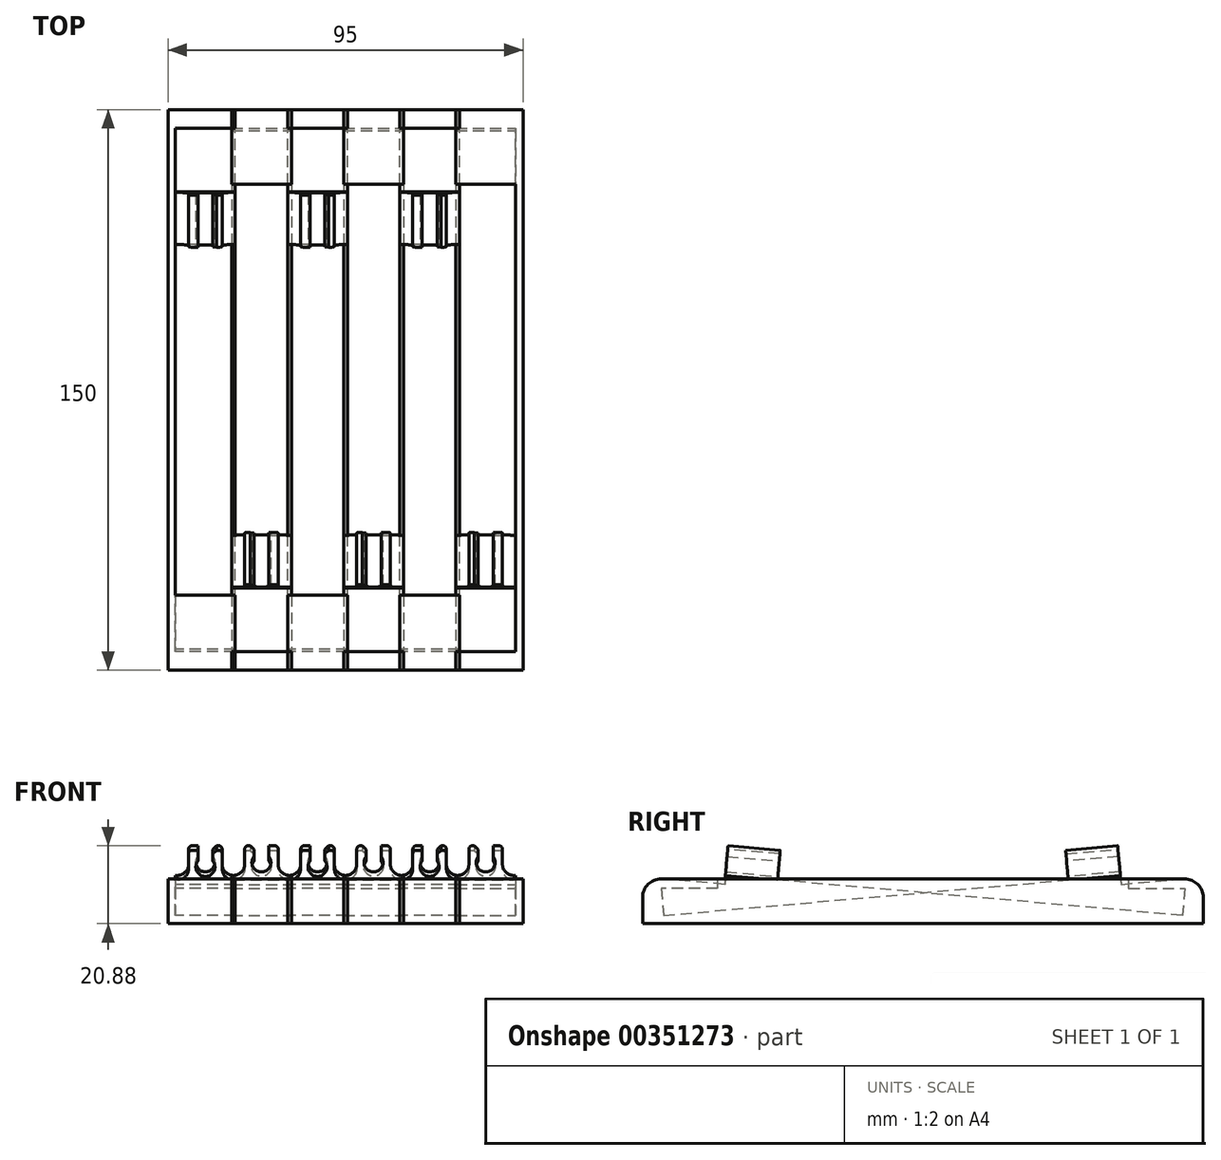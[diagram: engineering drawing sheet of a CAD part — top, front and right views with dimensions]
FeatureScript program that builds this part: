
annotation { "Feature Type Name" : "Feature", "Feature Type Description" : "" }
export const myFeature = defineFeature(function(context is Context, id is Id, definition is map)
    precondition{}
    {
        {
            var Q0;
            Q0=qCreatedBy(makeId("Right.planeOp"),FACE);
            var sketch = newSketch(context, id + "F0", { "sketchPlane" : qUnion([Q0])});
            skLineSegment(sketch, "E0", {"start": v(0, 0) * mm, "end": v(0, 7) * mm});
            skLineSegment(sketch, "E1", {"start": v(5, 12) * mm, "end": v(20, 12) * mm});
            skLineSegment(sketch, "E2", {"start": v(20, 12) * mm, "end": v(20, 9.5) * mm});
            skLineSegment(sketch, "E3", {"start": v(20, 9.5) * mm, "end": v(5.06, 8.2) * mm, "construction": true});
            skLineSegment(sketch, "E4", {"start": v(4.94, 9.5) * mm, "end": v(5.58, 2.22) * mm});
            skLineSegment(sketch, "E5", {"start": v(5.58, 2.22) * mm, "end": v(113.9, 11.7) * mm});
            skLineSegment(sketch, "E6", {"start": v(150, 7) * mm, "end": v(150, 0) * mm});
            skLineSegment(sketch, "E7", {"start": v(150, 0) * mm, "end": v(0, 0) * mm});
            skLineSegment(sketch, "E8", {"start": v(113.9, 11.7) * mm, "end": v(113.2, 19.66) * mm});
            skLineSegment(sketch, "E9", {"start": v(113.2, 19.66) * mm, "end": v(127.14, 20.88) * mm});
            skLineSegment(sketch, "E10", {"start": v(127.14, 20.88) * mm, "end": v(128.05, 10.52) * mm});
            skPoint(sketch, "E11.visualSharp", {"position": v(0, 12) * mm});
            skArc(sketch, "E11.filletArc", {"start": v(5, 12) * mm, "mid": v(1.46, 10.54) * mm, "end": v(0, 7) * mm});
            skPoint(sketch, "E12.visualSharp", {"position": v(150, 12) * mm});
            skLineSegment(sketch, "E13", {"start": v(20, 9.5) * mm, "end": v(4.94, 9.5) * mm});
            skLineSegment(sketch, "E14", {"start": v(128.05, 10.52) * mm, "end": v(145, 12) * mm});
            skLineSegment(sketch, "E15", {"start": v(145, 12) * mm, "end": v(145, 12) * mm});
            skArc(sketch, "E16.filletArc", {"start": v(150, 7) * mm, "mid": v(148.54, 10.54) * mm, "end": v(145, 12) * mm});
            skSolve(sketch);
        }
        {
            var Q0;
            Q0=qSketchRegion(id+"F0",true);
            extrude(context, id + "F1", {"entities" : qUnion([Q0]), "depth" : 16 * mm});
        }
        {
            var Q0;
            Q0=makeQuery(id+"F1.opExtrude","SWEPT_FACE",FACE,{"disambiguationData":[OSD([sQuery(id+"F0.wireOp",EDGE,"E8")])]});
            var sketch = newSketch(context, id + "F2", { "sketchPlane" : qUnion([Q0])});
            skLineSegment(sketch, "E17", {"start": v(8, 1.72) * mm, "end": v(8, 9.72) * mm, "construction": true});
            skArc(sketch, "E18", {"start": v(6, 6.8) * mm, "mid": v(8, 2.67) * mm, "end": v(10, 6.8) * mm});
            skLineSegment(sketch, "E19", {"start": v(12.5, 8.72) * mm, "end": v(12.5, 4.72) * mm});
            skLineSegment(sketch, "E20", {"start": v(15.5, 1.72) * mm, "end": v(18.5, 1.72) * mm});
            skLineSegment(sketch, "E21", {"start": v(18.5, 1.72) * mm, "end": v(18.5, 10.72) * mm});
            skLineSegment(sketch, "E22", {"start": v(3.5, 8.72) * mm, "end": v(3.5, 4.72) * mm});
            skLineSegment(sketch, "E23", {"start": v(0.5, 1.72) * mm, "end": v(-2.5, 1.72) * mm});
            skLineSegment(sketch, "E24", {"start": v(-2.5, 1.72) * mm, "end": v(-2.5, 10.72) * mm});
            skLineSegment(sketch, "E25", {"start": v(-2.5, 10.72) * mm, "end": v(18.5, 10.72) * mm});
            skLineSegment(sketch, "E26", {"start": v(8, 5.22) * mm, "end": v(6, 5.22) * mm, "construction": true});
            skLineSegment(sketch, "E27", {"start": v(6, 6.8) * mm, "end": v(6, 9.72) * mm});
            skLineSegment(sketch, "E28", {"start": v(8, 5.22) * mm, "end": v(10, 5.22) * mm, "construction": true});
            skLineSegment(sketch, "E29", {"start": v(10, 6.8) * mm, "end": v(10, 9.72) * mm});
            skPoint(sketch, "E30.orphan", {"position": v(3.5, 5.22) * mm});
            skPoint(sketch, "E31.orphan", {"position": v(12.5, 5.22) * mm});
            skLineSegment(sketch, "E32", {"start": v(6, 9.72) * mm, "end": v(4.5, 9.72) * mm});
            skLineSegment(sketch, "E33", {"start": v(10, 9.72) * mm, "end": v(11.5, 9.72) * mm});
            skPoint(sketch, "E34.visualSharp", {"position": v(3.5, 1.72) * mm});
            skArc(sketch, "E34.filletArc", {"start": v(0.5, 1.72) * mm, "mid": v(2.62, 2.6) * mm, "end": v(3.5, 4.72) * mm});
            skPoint(sketch, "E35.visualSharp", {"position": v(12.5, 1.72) * mm});
            skArc(sketch, "E35.filletArc", {"start": v(12.5, 4.72) * mm, "mid": v(13.38, 2.6) * mm, "end": v(15.5, 1.72) * mm});
            skPoint(sketch, "E36.visualSharp", {"position": v(3.5, 9.72) * mm});
            skArc(sketch, "E36.filletArc", {"start": v(4.5, 9.72) * mm, "mid": v(3.8, 9.43) * mm, "end": v(3.5, 8.72) * mm});
            skPoint(sketch, "E37.visualSharp", {"position": v(12.5, 9.72) * mm});
            skArc(sketch, "E37.filletArc", {"start": v(12.5, 8.72) * mm, "mid": v(12.2, 9.43) * mm, "end": v(11.5, 9.72) * mm});
            skSolve(sketch);
        }
        {
            var Q0;
            Q0=qSketchRegion(id+"F2",true);
            extrude(context, id + "F3", {"entities" : qUnion([Q0]), "operationType" : NewBodyOperationType.REMOVE, "oppositeDirection" : true, "depth" : 25 * mm});
        }
        {
            var Q0;
            Q0=makeQuery(id+"F3.boolean.opBoolean","COPY",EDGE,{"derivedFrom":makeQuery(id+"F3.opExtrude","SWEPT_EDGE",EDGE,{"disambiguationData":[OSD([sQuery(id+"F0.wireOp",EDGE,"E8"),sQuery(id+"F0.wireOp",EDGE,"E9"),sQuery(id+"F2.wireOp",EDGE,"E27"),sQuery(id+"F2.wireOp",EDGE,"E32")])]})});
            var Q1;
            Q1=makeQuery(id+"F3.boolean.opBoolean","COPY",EDGE,{"derivedFrom":makeQuery(id+"F3.opExtrude","SWEPT_EDGE",EDGE,{"disambiguationData":[OSD([sQuery(id+"F0.wireOp",EDGE,"E8"),sQuery(id+"F0.wireOp",EDGE,"E9"),sQuery(id+"F2.wireOp",EDGE,"E29"),sQuery(id+"F2.wireOp",EDGE,"E33")])]})});
            chamfer(context, id + "F4", {"entities" : qUnion([Q0, Q1]), "width" : 1 * mm, "tangentPropagation" : true});
        }
        {
            var Q0;
            Q0=makeQuery(id+"F1.opExtrude","SWEPT_BODY",BODY,{"disambiguationData":[OSD([sQuery(id+"F0.wireOp",EDGE,"E0"),sQuery(id+"F0.wireOp",EDGE,"E1"),sQuery(id+"F0.wireOp",EDGE,"E2"),sQuery(id+"F0.wireOp",EDGE,"E4"),sQuery(id+"F0.wireOp",EDGE,"E5"),sQuery(id+"F0.wireOp",EDGE,"E6"),sQuery(id+"F0.wireOp",EDGE,"E7"),sQuery(id+"F0.wireOp",EDGE,"E8"),sQuery(id+"F0.wireOp",EDGE,"E9"),sQuery(id+"F0.wireOp",EDGE,"E10"),sQuery(id+"F0.wireOp",EDGE,"Y9S6pfHg-R41R-CDvD-xWL7-1D2eYxtCf16d"),sQuery(id+"F0.wireOp",EDGE,"E11.filletArc"),sQuery(id+"F0.wireOp",EDGE,"E12.filletArc"),sQuery(id+"F0.wireOp",EDGE,"E13")])]});
            transform(context, id + "F5", {"entities" : qUnion([Q0]), "transformType" : TransformType.TRANSLATION_3D, "dx" : 30 * mm, "dy" : 0 * mm, "dz" : 0 * mm, "makeCopy" : true});
        }
        {
            var Q0;
            Q0=makeQuery(id+"F5.opPattern","COPY",BODY,{"derivedFrom":makeQuery(id+"F1.opExtrude","SWEPT_BODY",BODY,{"disambiguationData":[OSD([sQuery(id+"F0.wireOp",EDGE,"E0"),sQuery(id+"F0.wireOp",EDGE,"E1"),sQuery(id+"F0.wireOp",EDGE,"E2"),sQuery(id+"F0.wireOp",EDGE,"E4"),sQuery(id+"F0.wireOp",EDGE,"E5"),sQuery(id+"F0.wireOp",EDGE,"E6"),sQuery(id+"F0.wireOp",EDGE,"E7"),sQuery(id+"F0.wireOp",EDGE,"E8"),sQuery(id+"F0.wireOp",EDGE,"E9"),sQuery(id+"F0.wireOp",EDGE,"E10"),sQuery(id+"F0.wireOp",EDGE,"Y9S6pfHg-R41R-CDvD-xWL7-1D2eYxtCf16d"),sQuery(id+"F0.wireOp",EDGE,"E11.filletArc"),sQuery(id+"F0.wireOp",EDGE,"E12.filletArc"),sQuery(id+"F0.wireOp",EDGE,"E13")])]}),"instanceName":"1"});
            transform(context, id + "F6", {"entities" : qUnion([Q0]), "transformType" : TransformType.TRANSLATION_3D, "dx" : 30 * mm, "dy" : 0 * mm, "dz" : 0 * mm, "makeCopy" : true});
        }
        {
            var Q0;
            Q0=makeQuery(id+"F1.opExtrude","SWEPT_BODY",BODY,{"disambiguationData":[OSD([sQuery(id+"F0.wireOp",EDGE,"E0"),sQuery(id+"F0.wireOp",EDGE,"E1"),sQuery(id+"F0.wireOp",EDGE,"E2"),sQuery(id+"F0.wireOp",EDGE,"E4"),sQuery(id+"F0.wireOp",EDGE,"E5"),sQuery(id+"F0.wireOp",EDGE,"E6"),sQuery(id+"F0.wireOp",EDGE,"E7"),sQuery(id+"F0.wireOp",EDGE,"E8"),sQuery(id+"F0.wireOp",EDGE,"E9"),sQuery(id+"F0.wireOp",EDGE,"E10"),sQuery(id+"F0.wireOp",EDGE,"Y9S6pfHg-R41R-CDvD-xWL7-1D2eYxtCf16d"),sQuery(id+"F0.wireOp",EDGE,"E11.filletArc"),sQuery(id+"F0.wireOp",EDGE,"E12.filletArc"),sQuery(id+"F0.wireOp",EDGE,"E13")])]});
            transform(context, id + "F7", {"entities" : qUnion([Q0]), "transformType" : TransformType.TRANSLATION_3D, "dx" : 0 * mm, "dy" : 160 * mm, "dz" : 0 * mm, "makeCopy" : true});
        }
        {
            var Q0;
            Q0=makeQuery(id+"F5.opPattern","COPY",BODY,{"derivedFrom":makeQuery(id+"F1.opExtrude","SWEPT_BODY",BODY,{"disambiguationData":[OSD([sQuery(id+"F0.wireOp",EDGE,"E0"),sQuery(id+"F0.wireOp",EDGE,"E1"),sQuery(id+"F0.wireOp",EDGE,"E2"),sQuery(id+"F0.wireOp",EDGE,"E4"),sQuery(id+"F0.wireOp",EDGE,"E5"),sQuery(id+"F0.wireOp",EDGE,"E6"),sQuery(id+"F0.wireOp",EDGE,"E7"),sQuery(id+"F0.wireOp",EDGE,"E8"),sQuery(id+"F0.wireOp",EDGE,"E9"),sQuery(id+"F0.wireOp",EDGE,"E10"),sQuery(id+"F0.wireOp",EDGE,"Y9S6pfHg-R41R-CDvD-xWL7-1D2eYxtCf16d"),sQuery(id+"F0.wireOp",EDGE,"E11.filletArc"),sQuery(id+"F0.wireOp",EDGE,"E12.filletArc"),sQuery(id+"F0.wireOp",EDGE,"E13")])]}),"instanceName":"1"});
            transform(context, id + "F8", {"entities" : qUnion([Q0]), "transformType" : TransformType.TRANSLATION_3D, "dx" : 0 * mm, "dy" : 160 * mm, "dz" : 0 * mm, "makeCopy" : true});
        }
        {
            var Q0;
            Q0=makeQuery(id+"F6.opPattern","COPY",BODY,{"derivedFrom":makeQuery(id+"F5.opPattern","COPY",BODY,{"derivedFrom":makeQuery(id+"F1.opExtrude","SWEPT_BODY",BODY,{"disambiguationData":[OSD([sQuery(id+"F0.wireOp",EDGE,"E0"),sQuery(id+"F0.wireOp",EDGE,"E1"),sQuery(id+"F0.wireOp",EDGE,"E2"),sQuery(id+"F0.wireOp",EDGE,"E4"),sQuery(id+"F0.wireOp",EDGE,"E5"),sQuery(id+"F0.wireOp",EDGE,"E6"),sQuery(id+"F0.wireOp",EDGE,"E7"),sQuery(id+"F0.wireOp",EDGE,"E8"),sQuery(id+"F0.wireOp",EDGE,"E9"),sQuery(id+"F0.wireOp",EDGE,"E10"),sQuery(id+"F0.wireOp",EDGE,"Y9S6pfHg-R41R-CDvD-xWL7-1D2eYxtCf16d"),sQuery(id+"F0.wireOp",EDGE,"E11.filletArc"),sQuery(id+"F0.wireOp",EDGE,"E12.filletArc"),sQuery(id+"F0.wireOp",EDGE,"E13")])]}),"instanceName":"1"}),"instanceName":"1"});
            transform(context, id + "F9", {"entities" : qUnion([Q0]), "transformType" : TransformType.TRANSLATION_3D, "dx" : 0 * mm, "dy" : 160 * mm, "dz" : 0 * mm, "makeCopy" : true});
        }
        {
            var Q0;
            Q0=qCreatedBy(makeId("Right.planeOp"),FACE);
            var sketch = newSketch(context, id + "F10", { "sketchPlane" : qUnion([Q0])});
            skLineSegment(sketch, "E38", {"start": v(0, 0) * mm, "end": v(0, 50) * mm, "construction": true});
            skSolve(sketch);
        }
        {
            var Q0;
            Q0=makeQuery(id+"F8.opPattern","COPY",BODY,{"derivedFrom":makeQuery(id+"F5.opPattern","COPY",BODY,{"derivedFrom":makeQuery(id+"F1.opExtrude","SWEPT_BODY",BODY,{"disambiguationData":[OSD([sQuery(id+"F0.wireOp",EDGE,"E0"),sQuery(id+"F0.wireOp",EDGE,"E1"),sQuery(id+"F0.wireOp",EDGE,"E2"),sQuery(id+"F0.wireOp",EDGE,"E4"),sQuery(id+"F0.wireOp",EDGE,"E5"),sQuery(id+"F0.wireOp",EDGE,"E6"),sQuery(id+"F0.wireOp",EDGE,"E7"),sQuery(id+"F0.wireOp",EDGE,"E8"),sQuery(id+"F0.wireOp",EDGE,"E9"),sQuery(id+"F0.wireOp",EDGE,"E10"),sQuery(id+"F0.wireOp",EDGE,"Y9S6pfHg-R41R-CDvD-xWL7-1D2eYxtCf16d"),sQuery(id+"F0.wireOp",EDGE,"E11.filletArc"),sQuery(id+"F0.wireOp",EDGE,"E12.filletArc"),sQuery(id+"F0.wireOp",EDGE,"E13")])]}),"instanceName":"1"}),"instanceName":"1"});
            var Q1;
            Q1=makeQuery(id+"F9.opPattern","COPY",BODY,{"derivedFrom":makeQuery(id+"F6.opPattern","COPY",BODY,{"derivedFrom":makeQuery(id+"F5.opPattern","COPY",BODY,{"derivedFrom":makeQuery(id+"F1.opExtrude","SWEPT_BODY",BODY,{"disambiguationData":[OSD([sQuery(id+"F0.wireOp",EDGE,"E0"),sQuery(id+"F0.wireOp",EDGE,"E1"),sQuery(id+"F0.wireOp",EDGE,"E2"),sQuery(id+"F0.wireOp",EDGE,"E4"),sQuery(id+"F0.wireOp",EDGE,"E5"),sQuery(id+"F0.wireOp",EDGE,"E6"),sQuery(id+"F0.wireOp",EDGE,"E7"),sQuery(id+"F0.wireOp",EDGE,"E8"),sQuery(id+"F0.wireOp",EDGE,"E9"),sQuery(id+"F0.wireOp",EDGE,"E10"),sQuery(id+"F0.wireOp",EDGE,"Y9S6pfHg-R41R-CDvD-xWL7-1D2eYxtCf16d"),sQuery(id+"F0.wireOp",EDGE,"E11.filletArc"),sQuery(id+"F0.wireOp",EDGE,"E12.filletArc"),sQuery(id+"F0.wireOp",EDGE,"E13")])]}),"instanceName":"1"}),"instanceName":"1"}),"instanceName":"1"});
            var Q2;
            Q2=makeQuery(id+"F7.opPattern","COPY",BODY,{"derivedFrom":makeQuery(id+"F1.opExtrude","SWEPT_BODY",BODY,{"disambiguationData":[OSD([sQuery(id+"F0.wireOp",EDGE,"E0"),sQuery(id+"F0.wireOp",EDGE,"E1"),sQuery(id+"F0.wireOp",EDGE,"E2"),sQuery(id+"F0.wireOp",EDGE,"E4"),sQuery(id+"F0.wireOp",EDGE,"E5"),sQuery(id+"F0.wireOp",EDGE,"E6"),sQuery(id+"F0.wireOp",EDGE,"E7"),sQuery(id+"F0.wireOp",EDGE,"E8"),sQuery(id+"F0.wireOp",EDGE,"E9"),sQuery(id+"F0.wireOp",EDGE,"E10"),sQuery(id+"F0.wireOp",EDGE,"Y9S6pfHg-R41R-CDvD-xWL7-1D2eYxtCf16d"),sQuery(id+"F0.wireOp",EDGE,"E11.filletArc"),sQuery(id+"F0.wireOp",EDGE,"E12.filletArc"),sQuery(id+"F0.wireOp",EDGE,"E13")])]}),"instanceName":"1"});
            var Q3;
            Q3=sQuery(id+"F10.wireOp",EDGE,"E38");
            transform(context, id + "F11", {"entities" : qUnion([Q0, Q1, Q2]), "transformType" : TransformType.ROTATION, "transformAxis" : qUnion([Q3]), "angle" : 180 * degree, "makeCopy" : false});
        }
        {
            var Q0;
            Q0=makeQuery(id+"F7.opPattern","COPY",BODY,{"derivedFrom":makeQuery(id+"F1.opExtrude","SWEPT_BODY",BODY,{"disambiguationData":[OSD([sQuery(id+"F0.wireOp",EDGE,"E0"),sQuery(id+"F0.wireOp",EDGE,"E1"),sQuery(id+"F0.wireOp",EDGE,"E2"),sQuery(id+"F0.wireOp",EDGE,"E4"),sQuery(id+"F0.wireOp",EDGE,"E5"),sQuery(id+"F0.wireOp",EDGE,"E6"),sQuery(id+"F0.wireOp",EDGE,"E7"),sQuery(id+"F0.wireOp",EDGE,"E8"),sQuery(id+"F0.wireOp",EDGE,"E9"),sQuery(id+"F0.wireOp",EDGE,"E10"),sQuery(id+"F0.wireOp",EDGE,"Y9S6pfHg-R41R-CDvD-xWL7-1D2eYxtCf16d"),sQuery(id+"F0.wireOp",EDGE,"E11.filletArc"),sQuery(id+"F0.wireOp",EDGE,"E12.filletArc"),sQuery(id+"F0.wireOp",EDGE,"E13")])]}),"instanceName":"1"});
            var Q1;
            Q1=makeQuery(id+"F8.opPattern","COPY",BODY,{"derivedFrom":makeQuery(id+"F5.opPattern","COPY",BODY,{"derivedFrom":makeQuery(id+"F1.opExtrude","SWEPT_BODY",BODY,{"disambiguationData":[OSD([sQuery(id+"F0.wireOp",EDGE,"E0"),sQuery(id+"F0.wireOp",EDGE,"E1"),sQuery(id+"F0.wireOp",EDGE,"E2"),sQuery(id+"F0.wireOp",EDGE,"E4"),sQuery(id+"F0.wireOp",EDGE,"E5"),sQuery(id+"F0.wireOp",EDGE,"E6"),sQuery(id+"F0.wireOp",EDGE,"E7"),sQuery(id+"F0.wireOp",EDGE,"E8"),sQuery(id+"F0.wireOp",EDGE,"E9"),sQuery(id+"F0.wireOp",EDGE,"E10"),sQuery(id+"F0.wireOp",EDGE,"Y9S6pfHg-R41R-CDvD-xWL7-1D2eYxtCf16d"),sQuery(id+"F0.wireOp",EDGE,"E11.filletArc"),sQuery(id+"F0.wireOp",EDGE,"E12.filletArc"),sQuery(id+"F0.wireOp",EDGE,"E13")])]}),"instanceName":"1"}),"instanceName":"1"});
            var Q2;
            Q2=makeQuery(id+"F9.opPattern","COPY",BODY,{"derivedFrom":makeQuery(id+"F6.opPattern","COPY",BODY,{"derivedFrom":makeQuery(id+"F5.opPattern","COPY",BODY,{"derivedFrom":makeQuery(id+"F1.opExtrude","SWEPT_BODY",BODY,{"disambiguationData":[OSD([sQuery(id+"F0.wireOp",EDGE,"E0"),sQuery(id+"F0.wireOp",EDGE,"E1"),sQuery(id+"F0.wireOp",EDGE,"E2"),sQuery(id+"F0.wireOp",EDGE,"E4"),sQuery(id+"F0.wireOp",EDGE,"E5"),sQuery(id+"F0.wireOp",EDGE,"E6"),sQuery(id+"F0.wireOp",EDGE,"E7"),sQuery(id+"F0.wireOp",EDGE,"E8"),sQuery(id+"F0.wireOp",EDGE,"E9"),sQuery(id+"F0.wireOp",EDGE,"E10"),sQuery(id+"F0.wireOp",EDGE,"Y9S6pfHg-R41R-CDvD-xWL7-1D2eYxtCf16d"),sQuery(id+"F0.wireOp",EDGE,"E11.filletArc"),sQuery(id+"F0.wireOp",EDGE,"E12.filletArc"),sQuery(id+"F0.wireOp",EDGE,"E13")])]}),"instanceName":"1"}),"instanceName":"1"}),"instanceName":"1"});
            transform(context, id + "F12", {"entities" : qUnion([Q0, Q1, Q2]), "transformType" : TransformType.TRANSLATION_3D, "dx" : 91 * mm, "dy" : 310 * mm, "dz" : 0 * mm, "makeCopy" : false});
        }
        {
            var Q0;
            Q0=makeQuery(id+"F7.opPattern","COPY",FACE,{"derivedFrom":makeQuery(id+"F1.opExtrude","CAP_FACE",FACE,{"disambiguationData":[OSD([sQuery(id+"F0.wireOp",EDGE,"E0"),sQuery(id+"F0.wireOp",EDGE,"E1"),sQuery(id+"F0.wireOp",EDGE,"E2"),sQuery(id+"F0.wireOp",EDGE,"E4"),sQuery(id+"F0.wireOp",EDGE,"E5"),sQuery(id+"F0.wireOp",EDGE,"E6"),sQuery(id+"F0.wireOp",EDGE,"E7"),sQuery(id+"F0.wireOp",EDGE,"E8"),sQuery(id+"F0.wireOp",EDGE,"E9"),sQuery(id+"F0.wireOp",EDGE,"E10"),sQuery(id+"F0.wireOp",EDGE,"E11.filletArc"),sQuery(id+"F0.wireOp",EDGE,"E13"),sQuery(id+"F0.wireOp",EDGE,"E14"),sQuery(id+"F0.wireOp",EDGE,"E16.filletArc")])],"isStart":true}),"instanceName":"1"});
            var sketch = newSketch(context, id + "F13", { "sketchPlane" : qUnion([Q0])});
            skPoint(sketch, "E39.oppositeSnap0", {"position": v(150, 3.5) * mm});
            skLineSegment(sketch, "E39.bottom", {"start": v(0, 0) * mm, "end": v(150, 0) * mm});
            skLineSegment(sketch, "E39.top", {"start": v(5, 12) * mm, "end": v(145, 12) * mm});
            skLineSegment(sketch, "E39.left", {"start": v(0, 0) * mm, "end": v(0, 7) * mm});
            skLineSegment(sketch, "E39.right", {"start": v(150, 0) * mm, "end": v(150, 7) * mm});
            skPoint(sketch, "E40.visualSharp", {"position": v(0, 12) * mm});
            skArc(sketch, "E40.filletArc", {"start": v(5, 12) * mm, "mid": v(1.46, 10.54) * mm, "end": v(0, 7) * mm});
            skPoint(sketch, "E41.visualSharp", {"position": v(150, 12) * mm});
            skArc(sketch, "E41.filletArc", {"start": v(150, 7) * mm, "mid": v(148.54, 10.54) * mm, "end": v(145, 12) * mm});
            skSolve(sketch);
        }
        {
            var Q0;
            Q0=qSketchRegion(id+"F13",true);
            extrude(context, id + "F14", {"entities" : qUnion([Q0]), "operationType" : NewBodyOperationType.ADD, "depth" : 2 * mm});
        }
        {
            var Q0;
            Q0=makeQuery(id+"F1.opExtrude","CAP_FACE",FACE,{"disambiguationData":[OSD([sQuery(id+"F0.wireOp",EDGE,"E0"),sQuery(id+"F0.wireOp",EDGE,"E1"),sQuery(id+"F0.wireOp",EDGE,"E2"),sQuery(id+"F0.wireOp",EDGE,"E4"),sQuery(id+"F0.wireOp",EDGE,"E5"),sQuery(id+"F0.wireOp",EDGE,"E6"),sQuery(id+"F0.wireOp",EDGE,"E7"),sQuery(id+"F0.wireOp",EDGE,"E8"),sQuery(id+"F0.wireOp",EDGE,"E9"),sQuery(id+"F0.wireOp",EDGE,"E10"),sQuery(id+"F0.wireOp",EDGE,"E11.filletArc"),sQuery(id+"F0.wireOp",EDGE,"E13"),sQuery(id+"F0.wireOp",EDGE,"E14"),sQuery(id+"F0.wireOp",EDGE,"E16.filletArc")])],"isStart":true});
            var sketch = newSketch(context, id + "F15", { "sketchPlane" : qUnion([Q0])});
            skLineSegment(sketch, "E42.bottom", {"start": v(0, 0) * mm, "end": v(-150, 0) * mm});
            skLineSegment(sketch, "E42.top", {"start": v(-5, 12) * mm, "end": v(-145, 12) * mm});
            skLineSegment(sketch, "E42.left", {"start": v(0, 0) * mm, "end": v(0, 7) * mm});
            skLineSegment(sketch, "E42.right", {"start": v(-150, 0) * mm, "end": v(-150, 7) * mm});
            skPoint(sketch, "E43.visualSharp", {"position": v(-150, 12) * mm});
            skArc(sketch, "E43.filletArc", {"start": v(-145, 12) * mm, "mid": v(-148.54, 10.54) * mm, "end": v(-150, 7) * mm});
            skPoint(sketch, "E44.visualSharp", {"position": v(0, 12) * mm});
            skArc(sketch, "E44.filletArc", {"start": v(0, 7) * mm, "mid": v(-1.46, 10.54) * mm, "end": v(-5, 12) * mm});
            skSolve(sketch);
        }
        {
            var Q0;
            Q0=qSketchRegion(id+"F15",true);
            extrude(context, id + "F16", {"entities" : qUnion([Q0]), "operationType" : NewBodyOperationType.ADD, "depth" : 2 * mm});
        }
    });
